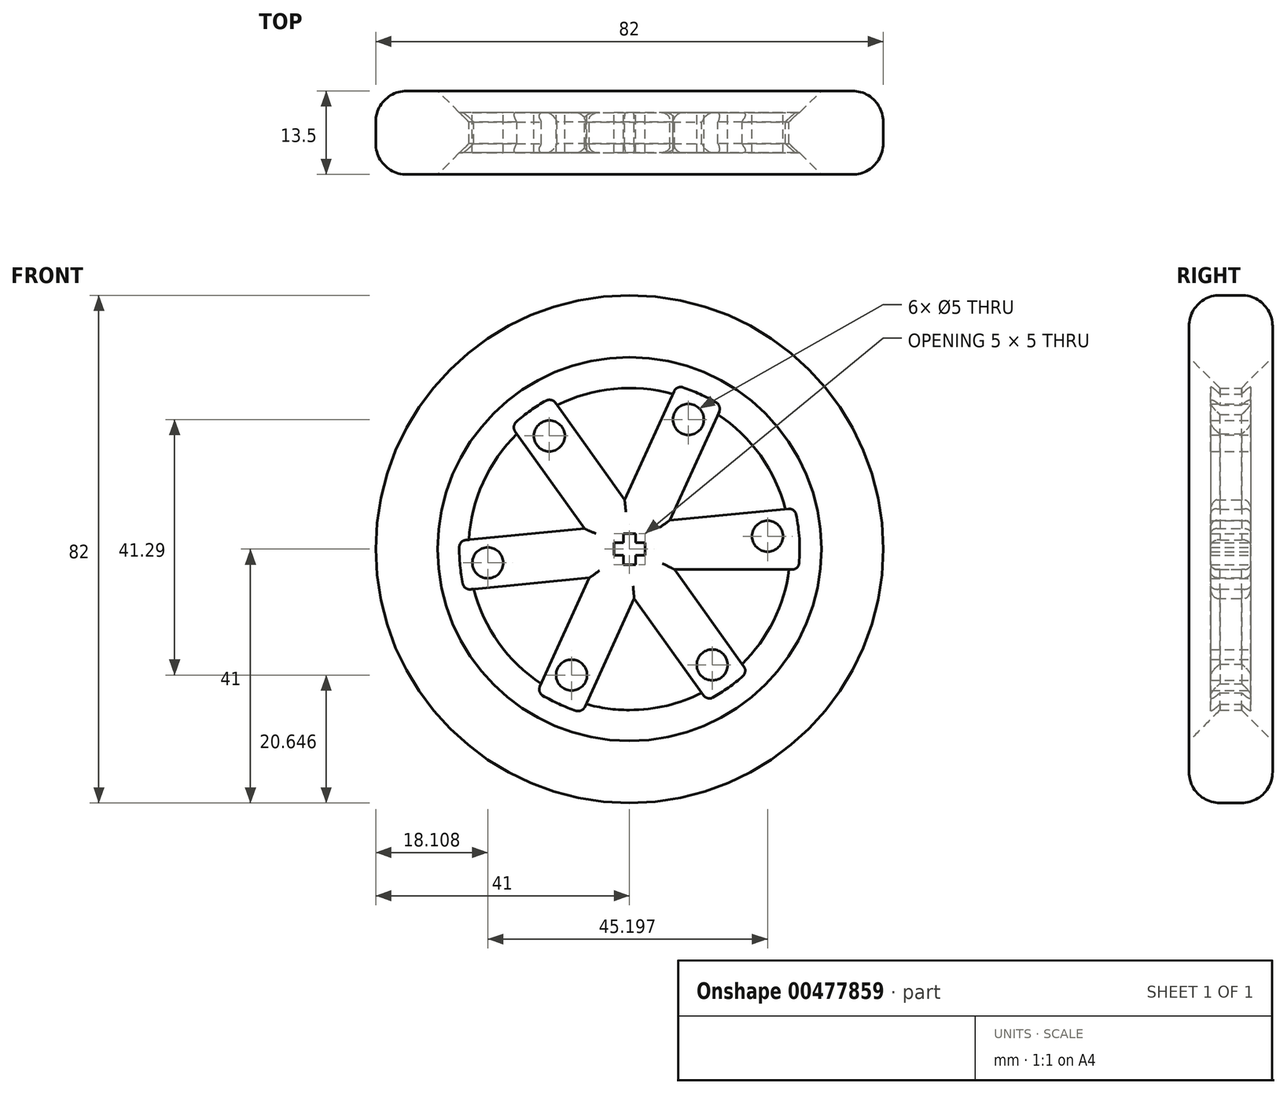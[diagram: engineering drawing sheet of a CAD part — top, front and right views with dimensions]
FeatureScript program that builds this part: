
annotation { "Feature Type Name" : "Feature", "Feature Type Description" : "" }
export const myFeature = defineFeature(function(context is Context, id is Id, definition is map)
    precondition{}
    {
        {
            var Q0;
            Q0=qCreatedBy(makeId("Front.planeOp"),FACE);
            var sketch = newSketch(context, id + "F0", { "sketchPlane" : qUnion([Q0])});
            skCircle(sketch, "E0", {"center": v(0, 0) * mm, "radius": 41 * mm});
            skCircle(sketch, "E1", {"center": v(0, 0) * mm, "radius": 6 * mm});
            skCircle(sketch, "E2", {"center": v(0, 0) * mm, "radius": 26 * mm});
            skCircle(sketch, "E3", {"center": v(0, 0) * mm, "radius": 30.5 * mm});
            skLineSegment(sketch, "E4", {"start": v(-18.18, 18.6) * mm, "end": v(-7.27, 3.31) * mm});
            skLineSegment(sketch, "E5.MirrorCS", {"start": v(-11.69, 23.23) * mm, "end": v(-0.78, 7.95) * mm});
            skLineSegment(sketch, "E6", {"start": v(7, 25.04) * mm, "end": v(-0.78, 7.95) * mm});
            skLineSegment(sketch, "E7.MirrorCS", {"start": v(14.28, 21.73) * mm, "end": v(6.5, 4.65) * mm});
            skLineSegment(sketch, "E8", {"start": v(25.19, 6.45) * mm, "end": v(6.5, 4.65) * mm});
            skLineSegment(sketch, "E9", {"start": v(-14.27, -21.73) * mm, "end": v(-6.5, -4.65) * mm});
            skLineSegment(sketch, "E10.MirrorCS", {"start": v(-7, -25.04) * mm, "end": v(0.77, -7.96) * mm});
            skCircle(sketch, "E11", {"center": v(-9.36, -20.35) * mm, "radius": 2.5 * mm});
            skCircle(sketch, "E12.1.0", {"center": v(22.3, 2.07) * mm, "radius": 2.5 * mm});
            skCircle(sketch, "E12.2.0", {"center": v(-12.95, 18.28) * mm, "radius": 2.5 * mm});
            skCircle(sketch, "E13", {"center": v(13.37, -18.71) * mm, "radius": 2.5 * mm});
            skCircle(sketch, "E14.1.0", {"center": v(9.52, 20.94) * mm, "radius": 2.5 * mm});
            skCircle(sketch, "E14.2.0", {"center": v(-22.9, -2.22) * mm, "radius": 2.5 * mm});
            skLineSegment(sketch, "E15.trimOffspring", {"start": v(4.85, -3.53) * mm, "end": v(4.84, -3.53) * mm});
            skLineSegment(sketch, "E16", {"start": v(0.77, -7.96) * mm, "end": v(11.67, -23.23) * mm});
            skLineSegment(sketch, "E17.MirrorCS", {"start": v(7.28, -3.3) * mm, "end": v(18.2, -18.57) * mm});
            skLineSegment(sketch, "E18", {"start": v(7.28, -3.3) * mm, "end": v(25.79, -3.3) * mm});
            skLineSegment(sketch, "E19", {"start": v(-7.27, 3.31) * mm, "end": v(-25.96, 1.5) * mm});
            skLineSegment(sketch, "E20", {"start": v(-6.5, -4.65) * mm, "end": v(-25.19, -6.46) * mm});
            skLineSegment(sketch, "E21", {"start": v(0, -2.5) * mm, "end": v(-1, -2.5) * mm});
            skLineSegment(sketch, "E22", {"start": v(-1, -2.5) * mm, "end": v(-1, -1) * mm});
            skLineSegment(sketch, "E23", {"start": v(-1, -1) * mm, "end": v(-2.5, -1) * mm});
            skLineSegment(sketch, "E24", {"start": v(-2.5, -1) * mm, "end": v(-2.5, 1) * mm});
            skLineSegment(sketch, "E25", {"start": v(-2.5, 1) * mm, "end": v(-1, 1) * mm});
            skLineSegment(sketch, "E26", {"start": v(-1, 1) * mm, "end": v(-1, 2.5) * mm});
            skLineSegment(sketch, "E27", {"start": v(-1, 2.5) * mm, "end": v(1, 2.5) * mm});
            skLineSegment(sketch, "E28", {"start": v(1, 2.5) * mm, "end": v(1, 1) * mm});
            skLineSegment(sketch, "E29", {"start": v(1, 1) * mm, "end": v(2.5, 1) * mm});
            skLineSegment(sketch, "E30", {"start": v(2.5, 1) * mm, "end": v(2.5, -1) * mm});
            skLineSegment(sketch, "E31", {"start": v(2.5, -1) * mm, "end": v(1, -1) * mm});
            skLineSegment(sketch, "E32", {"start": v(1, -1) * mm, "end": v(1, -2.5) * mm});
            skLineSegment(sketch, "E33", {"start": v(1, -2.5) * mm, "end": v(0, -2.5) * mm});
            skSolve(sketch);
        }
        {
            var Q0;
            Q0=makeQuery(id+"F0.imprint","IMPRINT",FACE,{"disambiguationData":[TD([[makeQuery(id+"F0.imprint","IMPRINT",EDGE,{"derivedFrom":sQuery(id+"F0.wireOp",EDGE,"E3")}),1.0]])]});
            var Q1;
            Q1=makeQuery(id+"F0.imprint","IMPRINT",FACE,{"disambiguationData":[TD([[makeQuery(id+"F0.imprint","IMPRINT",EDGE,{"derivedFrom":sQuery(id+"F0.wireOp",EDGE,"E0")}),1.0]])]});
            extrude(context, id + "F1", {"entities" : qUnion([Q0, Q1]), "endBound" : BoundingType.SYMMETRIC, "depth" : 13.5 * mm, "offsetDistance" : 25 * mm});
        }
        {
            var Q0;
            Q0=makeQuery(id+"F0.imprint","IMPRINT",FACE,{"disambiguationData":[TD([[makeQuery(id+"F0.imprint","IMPRINT",EDGE,{"derivedFrom":sQuery(id+"F0.wireOp",EDGE,"E1")}),-1.0]])]});
            var Q1;
            Q1=makeQuery(id+"F0.imprint","IMPRINT",FACE,{"disambiguationData":[TD([[makeQuery(id+"F0.imprint","IMPRINT",EDGE,{"derivedFrom":sQuery(id+"F0.wireOp",EDGE,"E1")}),1.0]])]});
            extrude(context, id + "F2", {"entities" : qUnion([Q0, Q1]), "operationType" : NewBodyOperationType.ADD, "endBound" : BoundingType.SYMMETRIC, "depth" : 6.5 * mm, "offsetDistance" : 25 * mm});
        }
        {
            var Q0;
            Q0=makeQuery(id+"F1.opExtrude","CAP_EDGE",EDGE,{"disambiguationData":[OSD([sQuery(id+"F0.wireOp",EDGE,"E0")])],"isStart":false});
            var Q1;
            Q1=makeQuery(id+"F1.opExtrude","CAP_EDGE",EDGE,{"disambiguationData":[OSD([sQuery(id+"F0.wireOp",EDGE,"E0")])],"isStart":true});
            fillet(context, id + "F3", {"entities" : qUnion([Q0, Q1]), "radius" : 5 * mm, "tangentPropagation" : true, "allowEdgeOverflow" : false});
        }
        {
            var Q0;
            Q0=makeQuery(id+"F1.opExtrude","CAP_EDGE",EDGE,{"disambiguationData":[OSD([sQuery(id+"F0.wireOp",EDGE,"E2")])],"isStart":true});
            var Q1;
            Q1=makeQuery(id+"F1.opExtrude","CAP_EDGE",EDGE,{"disambiguationData":[OSD([sQuery(id+"F0.wireOp",EDGE,"E2")])],"isStart":false});
            chamfer(context, id + "F4", {"entities" : qUnion([Q0, Q1]), "width" : 5 * mm, "tangentPropagation" : true});
        }
        {
            var Q0;
            Q0=makeQuery(id+"F2.opExtrude","CAP_EDGE",EDGE,{"disambiguationData":[OSD([sQuery(id+"F0.wireOp",EDGE,"E9")])],"isStart":true});
            var Q1;
            Q1=makeQuery(id+"F2.opExtrude","CAP_EDGE",EDGE,{"disambiguationData":[OSD([sQuery(id+"F0.wireOp",EDGE,"E20")])],"isStart":true});
            var Q2;
            Q2=makeQuery(id+"F2.opExtrude","CAP_EDGE",EDGE,{"disambiguationData":[OSD([sQuery(id+"F0.wireOp",EDGE,"E19")])],"isStart":true});
            var Q3;
            Q3=makeQuery(id+"F2.opExtrude","CAP_EDGE",EDGE,{"disambiguationData":[OSD([sQuery(id+"F0.wireOp",EDGE,"E4")])],"isStart":true});
            var Q4;
            Q4=makeQuery(id+"F2.opExtrude","CAP_EDGE",EDGE,{"disambiguationData":[OSD([sQuery(id+"F0.wireOp",EDGE,"E8")])],"isStart":true});
            var Q5;
            Q5=makeQuery(id+"F2.opExtrude","CAP_EDGE",EDGE,{"disambiguationData":[OSD([sQuery(id+"F0.wireOp",EDGE,"E18")])],"isStart":true});
            var Q6;
            Q6=makeQuery(id+"F2.opExtrude","CAP_EDGE",EDGE,{"disambiguationData":[OSD([sQuery(id+"F0.wireOp",EDGE,"E17.MirrorCS")])],"isStart":true});
            var Q7;
            Q7=makeQuery(id+"F2.opExtrude","CAP_EDGE",EDGE,{"disambiguationData":[OSD([sQuery(id+"F0.wireOp",EDGE,"E16")])],"isStart":true});
            var Q8;
            Q8=makeQuery(id+"F2.opExtrude","CAP_EDGE",EDGE,{"disambiguationData":[OSD([sQuery(id+"F0.wireOp",EDGE,"E10.MirrorCS")])],"isStart":true});
            var Q9;
            Q9=makeQuery(id+"F2.opExtrude","CAP_EDGE",EDGE,{"disambiguationData":[OSD([sQuery(id+"F0.wireOp",EDGE,"E5.MirrorCS")])],"isStart":true});
            var Q10;
            Q10=makeQuery(id+"F2.opExtrude","CAP_EDGE",EDGE,{"disambiguationData":[OSD([sQuery(id+"F0.wireOp",EDGE,"E6")])],"isStart":true});
            var Q11;
            Q11=makeQuery(id+"F2.opExtrude","CAP_EDGE",EDGE,{"disambiguationData":[OSD([sQuery(id+"F0.wireOp",EDGE,"E7.MirrorCS")])],"isStart":true});
            var Q12;
            Q12=makeQuery(id+"F2.opExtrude","CAP_EDGE",EDGE,{"disambiguationData":[OSD([sQuery(id+"F0.wireOp",EDGE,"E16")])],"isStart":false});
            var Q13;
            Q13=makeQuery(id+"F2.opExtrude","CAP_EDGE",EDGE,{"disambiguationData":[OSD([sQuery(id+"F0.wireOp",EDGE,"E10.MirrorCS")])],"isStart":false});
            var Q14;
            Q14=makeQuery(id+"F2.opExtrude","CAP_EDGE",EDGE,{"disambiguationData":[OSD([sQuery(id+"F0.wireOp",EDGE,"E9")])],"isStart":false});
            var Q15;
            Q15=makeQuery(id+"F2.opExtrude","CAP_EDGE",EDGE,{"disambiguationData":[OSD([sQuery(id+"F0.wireOp",EDGE,"E20")])],"isStart":false});
            var Q16;
            Q16=makeQuery(id+"F2.opExtrude","CAP_EDGE",EDGE,{"disambiguationData":[OSD([sQuery(id+"F0.wireOp",EDGE,"E19")])],"isStart":false});
            var Q17;
            Q17=makeQuery(id+"F2.opExtrude","CAP_EDGE",EDGE,{"disambiguationData":[OSD([sQuery(id+"F0.wireOp",EDGE,"E4")])],"isStart":false});
            var Q18;
            Q18=makeQuery(id+"F2.opExtrude","CAP_EDGE",EDGE,{"disambiguationData":[OSD([sQuery(id+"F0.wireOp",EDGE,"E5.MirrorCS")])],"isStart":false});
            var Q19;
            Q19=makeQuery(id+"F2.opExtrude","CAP_EDGE",EDGE,{"disambiguationData":[OSD([sQuery(id+"F0.wireOp",EDGE,"E6")])],"isStart":false});
            var Q20;
            Q20=makeQuery(id+"F2.opExtrude","CAP_EDGE",EDGE,{"disambiguationData":[OSD([sQuery(id+"F0.wireOp",EDGE,"E7.MirrorCS")])],"isStart":false});
            var Q21;
            Q21=makeQuery(id+"F2.opExtrude","CAP_EDGE",EDGE,{"disambiguationData":[OSD([sQuery(id+"F0.wireOp",EDGE,"E8")])],"isStart":false});
            var Q22;
            Q22=makeQuery(id+"F2.opExtrude","CAP_EDGE",EDGE,{"disambiguationData":[OSD([sQuery(id+"F0.wireOp",EDGE,"E18")])],"isStart":false});
            var Q23;
            Q23=makeQuery(id+"F2.opExtrude","CAP_EDGE",EDGE,{"disambiguationData":[OSD([sQuery(id+"F0.wireOp",EDGE,"E17.MirrorCS")])],"isStart":false});
            fillet(context, id + "F5", {"entities" : qUnion([Q0, Q1, Q2, Q3, Q4, Q5, Q6, Q7, Q8, Q9, Q10, Q11, Q12, Q13, Q14, Q15, Q16, Q17, Q18, Q19, Q20, Q21, Q22, Q23]), "radius" : 1 * mm, "tangentPropagation" : true, "allowEdgeOverflow" : false});
        }
    });
